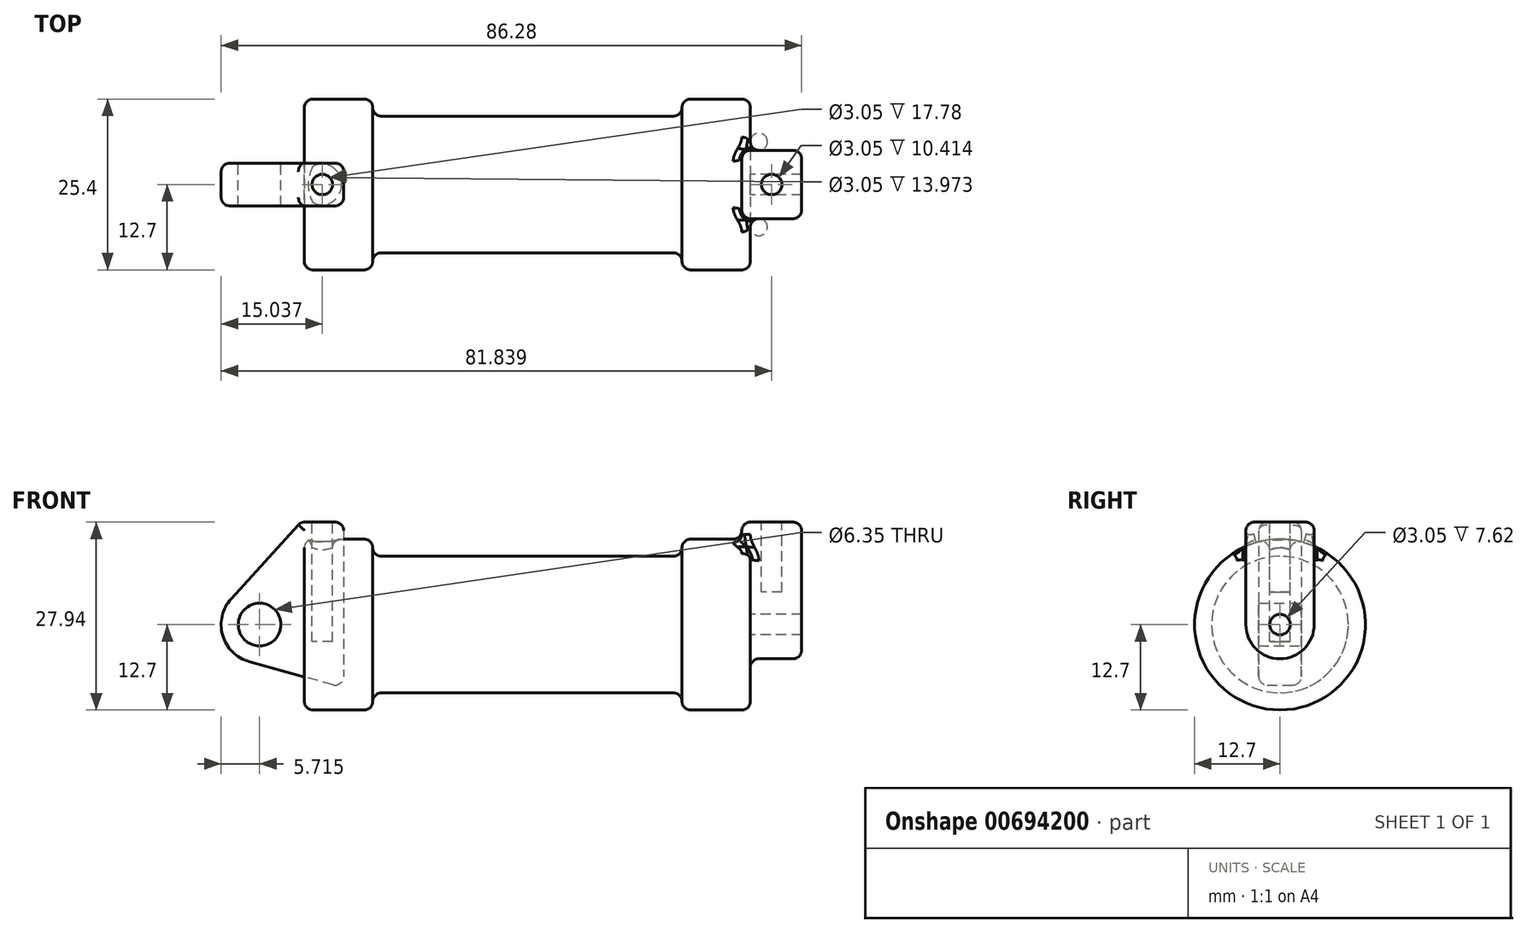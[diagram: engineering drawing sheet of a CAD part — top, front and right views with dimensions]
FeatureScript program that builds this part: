
annotation { "Feature Type Name" : "Feature", "Feature Type Description" : "" }
export const myFeature = defineFeature(function(context is Context, id is Id, definition is map)
    precondition{}
    {
        {
            var Q0;
            Q0=qCreatedBy(makeId("Front.planeOp"),FACE);
            var sketch = newSketch(context, id + "F0", { "sketchPlane" : qUnion([Q0])});
            skLineSegment(sketch, "E0", {"start": v(0, 0) * mm, "end": v(0, 12.7) * mm});
            skLineSegment(sketch, "E1", {"start": v(0, 12.7) * mm, "end": v(10.16, 12.7) * mm});
            skLineSegment(sketch, "E2", {"start": v(10.16, 12.7) * mm, "end": v(10.16, 10.16) * mm});
            skLineSegment(sketch, "E3", {"start": v(10.16, 10.16) * mm, "end": v(56.13, 10.16) * mm});
            skLineSegment(sketch, "E4", {"start": v(56.13, 10.16) * mm, "end": v(56.13, 12.7) * mm});
            skLineSegment(sketch, "E5", {"start": v(56.13, 12.7) * mm, "end": v(66.3, 12.7) * mm});
            skLineSegment(sketch, "E6", {"start": v(66.3, 12.7) * mm, "end": v(66.3, 0) * mm});
            skLineSegment(sketch, "E7", {"start": v(66.3, 0) * mm, "end": v(0, 0) * mm});
            skLineSegment(sketch, "E8", {"start": v(5.84, 15.24) * mm, "end": v(-0.5, 15.24) * mm});
            skLineSegment(sketch, "E9", {"start": v(-0.5, 15.24) * mm, "end": v(-10.88, 3.85) * mm});
            skLineSegment(sketch, "E10", {"start": v(0, 0) * mm, "end": v(-6.65, 0) * mm});
            skCircle(sketch, "E11", {"center": v(-6.65, 0) * mm, "radius": 5.72 * mm});
            skCircle(sketch, "E12", {"center": v(-6.65, 0) * mm, "radius": 3.18 * mm});
            skLineSegment(sketch, "E13", {"start": v(5.84, 15.24) * mm, "end": v(5.84, -9.4) * mm});
            skLineSegment(sketch, "E14", {"start": v(5.84, -9.4) * mm, "end": v(-8.18, -5.5) * mm});
            skSolve(sketch);
        }
        {
            var Q0;
            {var subQ0=sQuery(id+"F0.wireOp",EDGE,"E0");Q0=makeQuery(id+"F0.imprint","IMPRINT",FACE,{"disambiguationData":[TD([[makeQuery(id+"F0.imprint","IMPRINT",EDGE,{"derivedFrom":subQ0}),-1.0]])]});}
            var Q1;
            {var subQ0=sQuery(id+"F0.wireOp",EDGE,"E2");Q1=makeQuery(id+"F0.imprint","IMPRINT",FACE,{"disambiguationData":[TD([[makeQuery(id+"F0.imprint","IMPRINT",EDGE,{"derivedFrom":subQ0}),-1.0]])]});}
            var Q2;
            Q2=sQuery(id+"F0.wireOp",EDGE,"E7");
            revolve(context, id + "F1", {"entities" : qUnion([Q0, Q1]), "axis" : qUnion([Q2]), "revolveType" : RevolveType.FULL});
        }
        {
            var Q0;
            {var subQ1=sQuery(id+"F0.wireOp",EDGE,"E0");Q0=makeQuery(id+"F0.imprint","IMPRINT",FACE,{"disambiguationData":[TD([[makeQuery(id+"F0.imprint","IMPRINT",EDGE,{"derivedFrom":subQ1}),1.0]])]});}
            var Q1;
            {var subQ5=sQuery(id+"F0.wireOp",EDGE,"E12");Q1=makeQuery(id+"F0.imprint","IMPRINT",FACE,{"disambiguationData":[TD([[makeQuery(id+"F0.imprint","IMPRINT",EDGE,{"derivedFrom":subQ5}),-1.0]])]});}
            var Q2;
            {var subQ0=sQuery(id+"F0.wireOp",EDGE,"E14");Q2=makeQuery(id+"F0.imprint","IMPRINT",FACE,{"disambiguationData":[TD([[makeQuery(id+"F0.imprint","IMPRINT",EDGE,{"derivedFrom":subQ0}),-1.0]])]});}
            var Q3;
            {var subQ0=sQuery(id+"F0.wireOp",EDGE,"E0");Q3=makeQuery(id+"F0.imprint","IMPRINT",FACE,{"disambiguationData":[TD([[makeQuery(id+"F0.imprint","IMPRINT",EDGE,{"derivedFrom":subQ0}),-1.0]])]});}
            extrude(context, id + "F2", {"entities" : qUnion([Q0, Q1, Q2, Q3]), "endBound" : BoundingType.SYMMETRIC, "depth" : 6.35 * mm, "offsetDistance" : 25.4 * mm});
        }
        {
            var Q0;
            Q0=makeQuery(id+"F1.opRevolve","SWEPT_FACE",FACE,{"disambiguationData":[OSD([sQuery(id+"F0.wireOp",EDGE,"E6")])]});
            var sketch = newSketch(context, id + "F3", { "sketchPlane" : qUnion([Q0])});
            skCircle(sketch, "E15", {"center": v(0, 0) * mm, "radius": 1.52 * mm});
            skCircle(sketch, "E16", {"center": v(0, 0) * mm, "radius": 5.08 * mm});
            skLineSegment(sketch, "E17", {"start": v(5.08, 0) * mm, "end": v(5.08, 15.24) * mm});
            skLineSegment(sketch, "E18", {"start": v(5.08, 15.24) * mm, "end": v(-5.08, 15.24) * mm});
            skLineSegment(sketch, "E19", {"start": v(-5.08, 15.24) * mm, "end": v(-5.08, 0) * mm});
            skSolve(sketch);
        }
        {
            var Q0;
            {var subQ0=sQuery(id+"F3.wireOp",EDGE,"E18");Q0=makeQuery(id+"F3.imprint","IMPRINT",FACE,{"disambiguationData":[TD([[makeQuery(id+"F3.imprint","IMPRINT",EDGE,{"derivedFrom":subQ0}),1.0]])]});}
            var Q1;
            {var subQ0=sQuery(id+"F3.wireOp",EDGE,"E17");var subQ1=sQuery(id+"F3.wireOp",EDGE,"E16");var subQ2=makeQuery(id+"F3.imprint","INTERSECT",VERTEX,{"derivedFrom":[subQ1,subQ0]});Q1=makeQuery(id+"F3.imprint","IMPRINT",FACE,{"disambiguationData":[TD([[makeQuery(id+"F3.imprint","IMPRINT",EDGE,{"disambiguationData":[TD([[subQ2,-1.0]])],"derivedFrom":subQ1}),-1.0]])]});}
            var Q2;
            Q2=makeQuery(id+"F3.imprint","IMPRINT",FACE,{"disambiguationData":[TD([[makeQuery(id+"F3.imprint","IMPRINT",EDGE,{"derivedFrom":sQuery(id+"F3.wireOp",EDGE,"E15")}),-1.0]])]});
            extrude(context, id + "F4", {"entities" : qUnion([Q0, Q1, Q2]), "operationType" : NewBodyOperationType.ADD, "depth" : 7.62 * mm, "offsetDistance" : 25.4 * mm, "hasSecondDirection" : true, "secondDirectionOppositeDirection" : true, "secondDirectionDepth" : 1.27 * mm});
        }
        {
            var Q0;
            Q0=makeQuery(id+"F4.opExtrude","SWEPT_FACE",FACE,{"disambiguationData":[OSD([sQuery(id+"F3.wireOp",EDGE,"E18")])]});
            var sketch = newSketch(context, id + "F5", { "sketchPlane" : qUnion([Q0])});
            skLineSegment(sketch, "E20", {"start": v(69.47, 5.08) * mm, "end": v(69.47, -5.08) * mm, "construction": true});
            skLineSegment(sketch, "E21", {"start": v(65.02, 0) * mm, "end": v(73.91, 0) * mm, "construction": true});
            skCircle(sketch, "E22", {"center": v(69.47, 0) * mm, "radius": 1.52 * mm});
            skSolve(sketch);
        }
        {
            var Q0;
            Q0=makeQuery(id+"F5.imprint","IMPRINT",FACE,{"disambiguationData":[TD([[makeQuery(id+"F5.imprint","IMPRINT",EDGE,{"derivedFrom":sQuery(id+"F5.wireOp",EDGE,"E22")}),1.0]])]});
            extrude(context, id + "F6", {"entities" : qUnion([Q0]), "operationType" : NewBodyOperationType.REMOVE, "oppositeDirection" : true, "depth" : 10.4 * mm, "offsetDistance" : 25.4 * mm});
        }
        {
            var Q0;
            Q0=makeQuery(id+"F2.opExtrude","SWEPT_FACE",FACE,{"disambiguationData":[OSD([sQuery(id+"F0.wireOp",EDGE,"E8")])]});
            var sketch = newSketch(context, id + "F7", { "sketchPlane" : qUnion([Q0])});
            skLineSegment(sketch, "E23", {"start": v(2.67, 3.18) * mm, "end": v(2.67, -3.18) * mm, "construction": true});
            skLineSegment(sketch, "E24", {"start": v(-0.5, 0) * mm, "end": v(5.84, 0) * mm, "construction": true});
            skCircle(sketch, "E25", {"center": v(2.67, 0) * mm, "radius": 1.52 * mm});
            skSolve(sketch);
        }
        {
            var Q0;
            Q0=makeQuery(id+"F7.imprint","IMPRINT",FACE,{"disambiguationData":[TD([[makeQuery(id+"F7.imprint","IMPRINT",EDGE,{"derivedFrom":sQuery(id+"F7.wireOp",EDGE,"E25")}),1.0]])]});
            var Q1;
            Q1=sQuery(id+"F7.wireOp",EDGE,"E25");
            extrude(context, id + "F8", {"entities" : qUnion([Q0]), "operationType" : NewBodyOperationType.REMOVE, "surfaceEntities" : qUnion([Q1]), "oppositeDirection" : true, "depth" : 17.78 * mm, "offsetDistance" : 25.4 * mm});
        }
        {
            var Q0;
            Q0=makeQuery(id+"F1.opRevolve","SWEPT_FACE",FACE,{"disambiguationData":[OSD([sQuery(id+"F0.wireOp",EDGE,"E2")])]});
            var Q1;
            Q1=makeQuery(id+"F1.opRevolve","SWEPT_FACE",FACE,{"disambiguationData":[OSD([sQuery(id+"F0.wireOp",EDGE,"E4")])]});
            var Q2;
            Q2=makeQuery(id+"F1.opRevolve","SWEPT_FACE",FACE,{"disambiguationData":[OSD([sQuery(id+"F0.wireOp",EDGE,"E0")])]});
            var Q3;
            Q3=makeQuery(id+"F1.opRevolve","SWEPT_FACE",FACE,{"disambiguationData":[OSD([sQuery(id+"F0.wireOp",EDGE,"E1")])]});
            var Q4;
            Q4=makeQuery(id+"F1.opRevolve","SWEPT_FACE",FACE,{"disambiguationData":[OSD([sQuery(id+"F0.wireOp",EDGE,"E5")])]});
            var Q5;
            Q5=makeQuery(id+"F4.boolean.opBoolean","SPLIT",FACE,{"disambiguationData":[TD([makeQuery(id+"F1.opRevolve","SWEPT_FACE",FACE,{"disambiguationData":[OSD([sQuery(id+"F0.wireOp",EDGE,"E5")])]})])],"derivedFrom":makeQuery(id+"F1.opRevolve","SWEPT_FACE",FACE,{"disambiguationData":[OSD([sQuery(id+"F0.wireOp",EDGE,"E6")])]})});
            var Q6;
            Q6=makeQuery(id+"F4.opExtrude","SWEPT_FACE",FACE,{"disambiguationData":[OSD([sQuery(id+"F3.wireOp",EDGE,"E19")])]});
            var Q7;
            Q7=makeQuery(id+"F4.opExtrude","SWEPT_FACE",FACE,{"disambiguationData":[OSD([sQuery(id+"F3.wireOp",EDGE,"E17")])]});
            var Q8;
            Q8=makeQuery(id+"F4.opExtrude","SWEPT_FACE",FACE,{"disambiguationData":[OSD([sQuery(id+"F3.wireOp",EDGE,"E16")])]});
            var Q9;
            Q9=makeQuery(id+"F4.opExtrude","CAP_FACE",FACE,{"disambiguationData":[OSD([sQuery(id+"F3.wireOp",EDGE,"E15"),sQuery(id+"F3.wireOp",EDGE,"E16"),sQuery(id+"F3.wireOp",EDGE,"E17"),sQuery(id+"F3.wireOp",EDGE,"E18"),sQuery(id+"F3.wireOp",EDGE,"E19")])],"isStart":true});
            var Q10;
            Q10=makeQuery(id+"F2.opExtrude","SWEPT_FACE",FACE,{"disambiguationData":[OSD([sQuery(id+"F0.wireOp",EDGE,"E13")])]});
            var Q11;
            Q11=makeQuery(id+"F2.opExtrude","SWEPT_FACE",FACE,{"disambiguationData":[OSD([sQuery(id+"F0.wireOp",EDGE,"E11")])]});
            var Q12;
            Q12=makeQuery(id+"F2.opExtrude","SWEPT_FACE",FACE,{"disambiguationData":[OSD([sQuery(id+"F0.wireOp",EDGE,"E9")])]});
            var Q13;
            Q13=makeQuery(id+"F2.opExtrude","SWEPT_FACE",FACE,{"disambiguationData":[OSD([sQuery(id+"F0.wireOp",EDGE,"E14")])]});
            fillet(context, id + "F9", {"entities" : qUnion([Q0, Q1, Q2, Q3, Q4, Q5, Q6, Q7, Q8, Q9, Q10, Q11, Q12, Q13]), "radius" : 1.27 * mm, "tangentPropagation" : true, "allowEdgeOverflow" : false});
        }
        {
            var Q0;
            Q0=makeQuery(id+"F2.opExtrude","CAP_EDGE",EDGE,{"disambiguationData":[OSD([sQuery(id+"F0.wireOp",EDGE,"E8")])],"isStart":false});
            var Q1;
            Q1=makeQuery(id+"F2.opExtrude","CAP_EDGE",EDGE,{"disambiguationData":[OSD([sQuery(id+"F0.wireOp",EDGE,"E8")])],"isStart":true});
            var Q2;
            Q2=makeQuery(id+"F4.opExtrude","CAP_EDGE",EDGE,{"disambiguationData":[OSD([sQuery(id+"F3.wireOp",EDGE,"E18")])],"isStart":false});
            fillet(context, id + "F10", {"entities" : qUnion([Q0, Q1, Q2]), "radius" : 1.27 * mm, "tangentPropagation" : true, "allowEdgeOverflow" : false});
        }
    });
